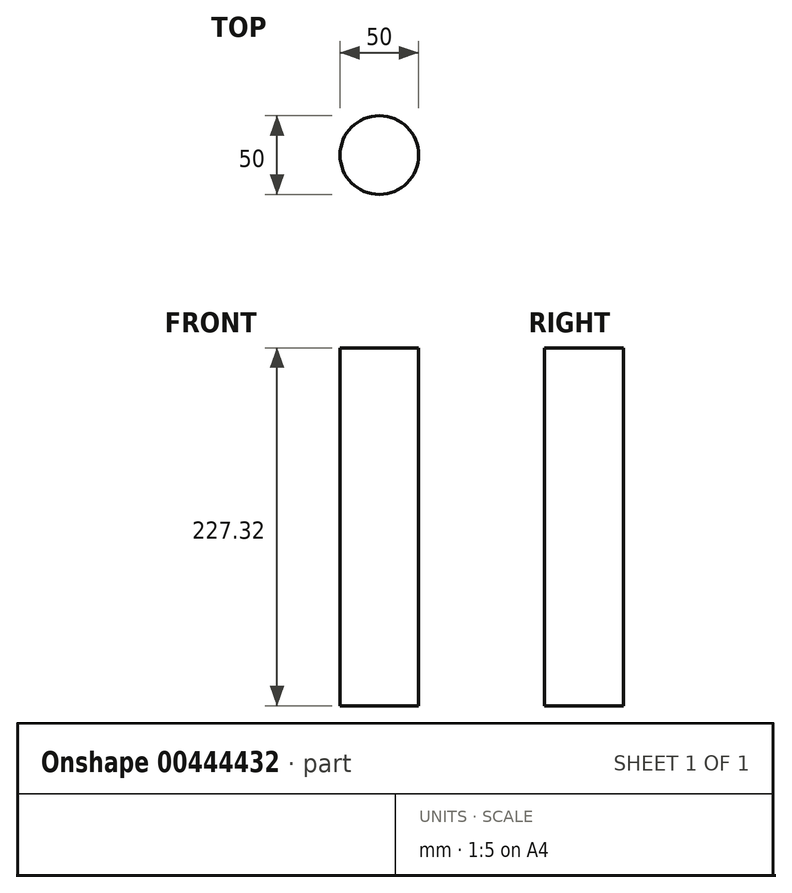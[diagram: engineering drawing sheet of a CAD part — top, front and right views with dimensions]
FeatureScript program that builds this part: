
annotation { "Feature Type Name" : "Feature", "Feature Type Description" : "" }
export const myFeature = defineFeature(function(context is Context, id is Id, definition is map)
    precondition{}
    {
        {
            var Q0;
            Q0=qCreatedBy(makeId("Top.planeOp"),FACE);
            var sketch = newSketch(context, id + "F0", { "sketchPlane" : qUnion([Q0])});
            skCircle(sketch, "E0", {"center": v(0, 0) * mm, "radius": 25 * mm});
            skSolve(sketch);
        }
        {
            var Q0;
            Q0=makeQuery(id+"F0.imprint","IMPRINT",FACE,{"disambiguationData":[TD([[makeQuery(id+"F0.imprint","IMPRINT",EDGE,{"derivedFrom":sQuery(id+"F0.wireOp",EDGE,"E0")}),1.0]])]});
            extrude(context, id + "F1", {"entities" : qUnion([Q0]), "depth" : 227.32 * mm, "offsetDistance" : 25 * mm});
        }
    });
